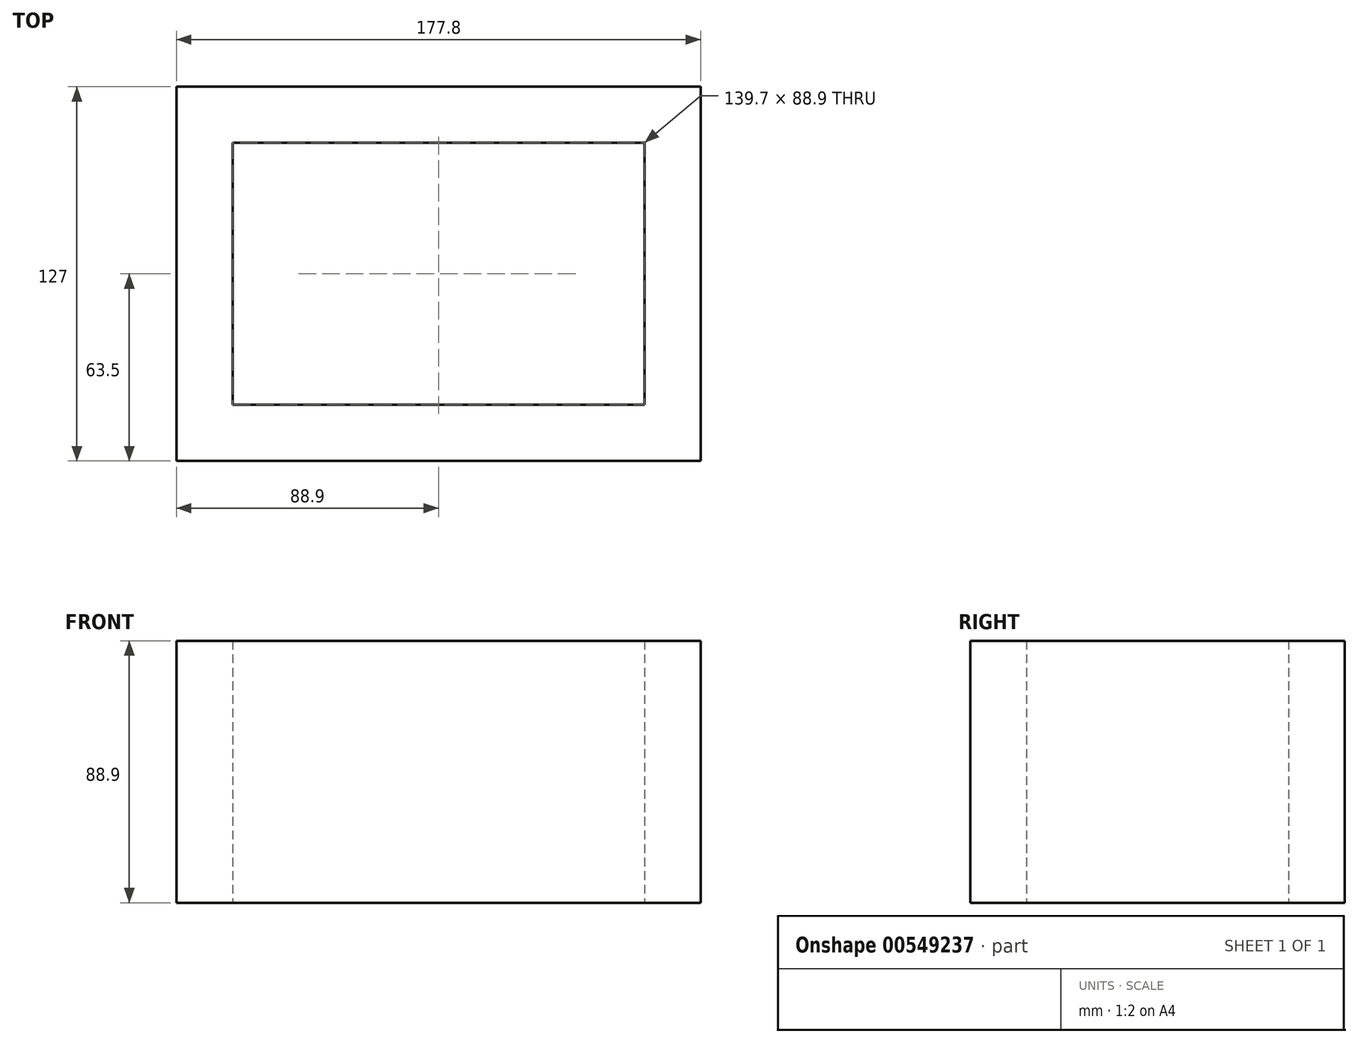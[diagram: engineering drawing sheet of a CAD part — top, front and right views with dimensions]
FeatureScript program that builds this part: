
annotation { "Feature Type Name" : "Feature", "Feature Type Description" : "" }
export const myFeature = defineFeature(function(context is Context, id is Id, definition is map)
    precondition{}
    {
        {
            var Q0;
            Q0=qCreatedBy(makeId("Top.planeOp"),FACE);
            var sketch = newSketch(context, id + "F0", { "sketchPlane" : qUnion([Q0])});
            skLineSegment(sketch, "E0.bottom", {"start": v(-88.9, 63.5) * mm, "end": v(88.9, 63.5) * mm});
            skLineSegment(sketch, "E0.top", {"start": v(-88.9, -63.5) * mm, "end": v(88.9, -63.5) * mm});
            skLineSegment(sketch, "E0.left", {"start": v(-88.9, 63.5) * mm, "end": v(-88.9, -63.5) * mm});
            skLineSegment(sketch, "E0.right", {"start": v(88.9, 63.5) * mm, "end": v(88.9, -63.5) * mm});
            skLineSegment(sketch, "E1.bottom", {"start": v(-69.85, 44.45) * mm, "end": v(69.85, 44.45) * mm});
            skLineSegment(sketch, "E1.top", {"start": v(-69.85, -44.45) * mm, "end": v(69.85, -44.45) * mm});
            skLineSegment(sketch, "E1.left", {"start": v(-69.85, 44.45) * mm, "end": v(-69.85, -44.45) * mm});
            skLineSegment(sketch, "E1.right", {"start": v(69.85, 44.45) * mm, "end": v(69.85, -44.45) * mm});
            skLineSegment(sketch, "E2", {"start": v(0, 44.45) * mm, "end": v(0, -44.45) * mm, "construction": true});
            skLineSegment(sketch, "E3", {"start": v(-69.85, 0) * mm, "end": v(69.85, 0) * mm, "construction": true});
            skPoint(sketch, "E3.startSnap0", {"position": v(-69.85, 0) * mm});
            skLineSegment(sketch, "E4", {"start": v(-88.9, 0) * mm, "end": v(-69.85, 0) * mm, "construction": true});
            skLineSegment(sketch, "E5", {"start": v(69.85, 0) * mm, "end": v(88.9, 0) * mm, "construction": true});
            skLineSegment(sketch, "E6", {"start": v(0, 44.45) * mm, "end": v(0, 63.5) * mm, "construction": true});
            skLineSegment(sketch, "E7", {"start": v(0, -44.45) * mm, "end": v(0, -63.5) * mm, "construction": true});
            skLineSegment(sketch, "E8", {"start": v(-69.85, 44.45) * mm, "end": v(-88.9, 44.45) * mm});
            skLineSegment(sketch, "E9", {"start": v(-69.85, -44.45) * mm, "end": v(-88.9, -44.45) * mm});
            skLineSegment(sketch, "E10", {"start": v(69.85, 44.45) * mm, "end": v(88.9, 44.45) * mm});
            skLineSegment(sketch, "E11", {"start": v(69.85, -44.45) * mm, "end": v(88.9, -44.45) * mm});
            skSolve(sketch);
        }
        {
            var Q0;
            {var subQ1=sQuery(id+"F0.wireOp",EDGE,"E0.bottom");Q0=makeQuery(id+"F0.imprint","IMPRINT",FACE,{"disambiguationData":[TD([[makeQuery(id+"F0.imprint","IMPRINT",EDGE,{"derivedFrom":subQ1}),-1.0]])]});}
            var Q1;
            {var subQ1=sQuery(id+"F0.wireOp",EDGE,"E0.top");Q1=makeQuery(id+"F0.imprint","IMPRINT",FACE,{"disambiguationData":[TD([[makeQuery(id+"F0.imprint","IMPRINT",EDGE,{"derivedFrom":subQ1}),1.0]])]});}
            extrude(context, id + "F1", {"entities" : qUnion([Q0, Q1]), "depth" : 88.9 * mm, "offsetDistance" : 25.4 * mm});
        }
        {
            var Q0;
            Q0=makeQuery(id+"F0.imprint","IMPRINT",FACE,{"disambiguationData":[TD([[makeQuery(id+"F0.imprint","IMPRINT",EDGE,{"derivedFrom":sQuery(id+"F0.wireOp",EDGE,"E1.left")}),-1.0]])]});
            var Q1;
            Q1=makeQuery(id+"F0.imprint","IMPRINT",FACE,{"disambiguationData":[TD([[makeQuery(id+"F0.imprint","IMPRINT",EDGE,{"derivedFrom":sQuery(id+"F0.wireOp",EDGE,"E1.right")}),1.0]])]});
            extrude(context, id + "F2", {"entities" : qUnion([Q0, Q1]), "operationType" : NewBodyOperationType.ADD, "depth" : 88.9 * mm, "offsetDistance" : 25.4 * mm});
        }
    });
